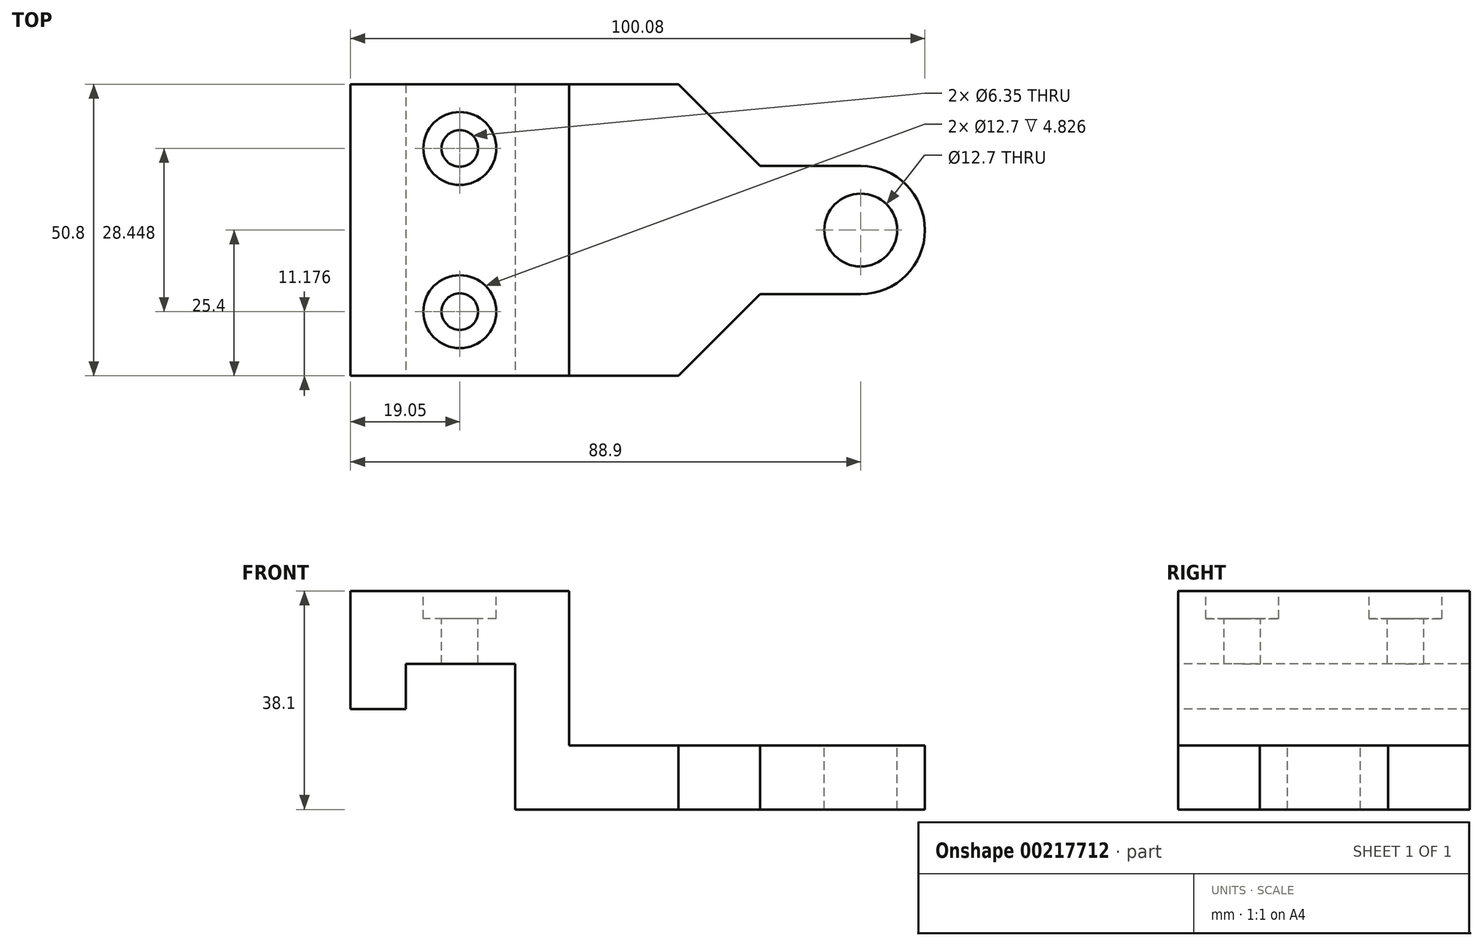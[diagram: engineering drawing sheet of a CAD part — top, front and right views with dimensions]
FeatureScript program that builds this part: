
annotation { "Feature Type Name" : "Feature", "Feature Type Description" : "" }
export const myFeature = defineFeature(function(context is Context, id is Id, definition is map)
    precondition{}
    {
        {
            var Q0;
            Q0=qCreatedBy(makeId("Right.planeOp"),FACE);
            var sketch = newSketch(context, id + "F0", { "sketchPlane" : qUnion([Q0])});
            skLineSegment(sketch, "E0.bottom", {"start": v(25.4, -19.05) * mm, "end": v(-25.4, -19.05) * mm});
            skLineSegment(sketch, "E0.top", {"start": v(25.4, 19.05) * mm, "end": v(-25.4, 19.05) * mm});
            skLineSegment(sketch, "E0.left", {"start": v(25.4, -19.05) * mm, "end": v(25.4, 19.05) * mm});
            skLineSegment(sketch, "E0.right", {"start": v(-25.4, -19.05) * mm, "end": v(-25.4, 19.05) * mm});
            skPoint(sketch, "E0.middle", {"position": v(0, 0) * mm});
            skSolve(sketch);
        }
        {
            var Q0;
            Q0=makeQuery(id+"F0.imprint","IMPRINT",FACE,{"disambiguationData":[TD([[makeQuery(id+"F0.imprint","IMPRINT",EDGE,{"derivedFrom":sQuery(id+"F0.wireOp",EDGE,"E0.bottom")}),-1.0]])]});
            extrude(context, id + "F1", {"entities" : qUnion([Q0]), "endBound" : BoundingType.SYMMETRIC, "depth" : 101.6 * mm});
        }
        {
            var Q0;
            Q0=makeQuery(id+"F1.opExtrude","SWEPT_FACE",FACE,{"disambiguationData":[OSD([sQuery(id+"F0.wireOp",EDGE,"E0.top")])]});
            var sketch = newSketch(context, id + "F2", { "sketchPlane" : qUnion([Q0])});
            skCircle(sketch, "E1", {"center": v(-31.75, -14.22) * mm, "radius": 3.18 * mm});
            skCircle(sketch, "E2", {"center": v(-31.75, 14.22) * mm, "radius": 3.18 * mm});
            skSolve(sketch);
        }
        {
            var Q0;
            Q0=makeQuery(id+"F2.imprint","IMPRINT",FACE,{"disambiguationData":[TD([[makeQuery(id+"F2.imprint","IMPRINT",EDGE,{"derivedFrom":sQuery(id+"F2.wireOp",EDGE,"E1")}),1.0]])]});
            var Q1;
            Q1=makeQuery(id+"F2.imprint","IMPRINT",FACE,{"disambiguationData":[TD([[makeQuery(id+"F2.imprint","IMPRINT",EDGE,{"derivedFrom":sQuery(id+"F2.wireOp",EDGE,"E2")}),1.0]])]});
            extrude(context, id + "F3", {"entities" : qUnion([Q0, Q1]), "operationType" : NewBodyOperationType.REMOVE, "endBound" : BoundingType.THROUGH_ALL, "oppositeDirection" : true, "depth" : 25.4 * mm});
        }
        {
            var Q0;
            Q0=makeQuery(id+"F1.opExtrude","SWEPT_FACE",FACE,{"disambiguationData":[OSD([sQuery(id+"F0.wireOp",EDGE,"E0.right")])]});
            var sketch = newSketch(context, id + "F4", { "sketchPlane" : qUnion([Q0])});
            skLineSegment(sketch, "E3", {"start": v(-50.8, 19.05) * mm, "end": v(-50.8, -1.52) * mm});
            skLineSegment(sketch, "E4", {"start": v(-50.8, -1.52) * mm, "end": v(-41.15, -1.52) * mm});
            skLineSegment(sketch, "E5", {"start": v(-50.8, 19.05) * mm, "end": v(-12.7, 19.05) * mm});
            skLineSegment(sketch, "E6", {"start": v(-12.7, -7.87) * mm, "end": v(50.8, -7.87) * mm});
            skLineSegment(sketch, "E7", {"start": v(50.8, -7.87) * mm, "end": v(50.8, 19.05) * mm});
            skLineSegment(sketch, "E8", {"start": v(50.8, 19.05) * mm, "end": v(-12.7, 19.05) * mm});
            skLineSegment(sketch, "E9", {"start": v(-41.15, -1.52) * mm, "end": v(-41.15, 6.35) * mm});
            skLineSegment(sketch, "E10", {"start": v(-41.15, 6.35) * mm, "end": v(-22.1, 6.35) * mm});
            skLineSegment(sketch, "E11", {"start": v(-22.1, 6.35) * mm, "end": v(-22.1, -19.05) * mm});
            skLineSegment(sketch, "E12", {"start": v(-22.1, -19.05) * mm, "end": v(-12.7, -19.05) * mm});
            skLineSegment(sketch, "E13", {"start": v(-12.7, -7.87) * mm, "end": v(-12.7, 19.05) * mm});
            skSolve(sketch);
        }
        {
            var Q0;
            {var subQ1=sQuery(id+"F4.wireOp",EDGE,"E4");Q0=makeQuery(id+"F4.imprint","IMPRINT",FACE,{"disambiguationData":[TD([[makeQuery(id+"F4.imprint","IMPRINT",EDGE,{"derivedFrom":subQ1}),-1.0]])]});}
            var Q1;
            Q1=makeQuery(id+"F4.imprint","IMPRINT",FACE,{"disambiguationData":[TD([[makeQuery(id+"F4.imprint","IMPRINT",EDGE,{"derivedFrom":sQuery(id+"F4.wireOp",EDGE,"E6")}),1.0]])]});
            extrude(context, id + "F5", {"entities" : qUnion([Q0, Q1]), "operationType" : NewBodyOperationType.REMOVE, "endBound" : BoundingType.THROUGH_ALL, "oppositeDirection" : true, "depth" : 25.4 * mm});
        }
        {
            var Q0;
            Q0=makeQuery(id+"F5.boolean.opBoolean","COPY",FACE,{"derivedFrom":makeQuery(id+"F5.opExtrude","SWEPT_FACE",FACE,{"disambiguationData":[OSD([sQuery(id+"F4.wireOp",EDGE,"E6")])]})});
            var sketch = newSketch(context, id + "F6", { "sketchPlane" : qUnion([Q0])});
            skPoint(sketch, "E14.endSnap0", {"position": v(-12.7, 0) * mm});
            skCircle(sketch, "E15", {"center": v(38.1, 0) * mm, "radius": 6.35 * mm});
            skArc(sketch, "E16", {"start": v(38.1, -11.18) * mm, "mid": v(49.28, 0) * mm, "end": v(38.1, 11.18) * mm});
            skLineSegment(sketch, "E17", {"start": v(-12.7, -25.4) * mm, "end": v(6.35, -25.4) * mm});
            skLineSegment(sketch, "E18", {"start": v(6.35, -25.4) * mm, "end": v(6.35, 25.4) * mm});
            skLineSegment(sketch, "E19", {"start": v(38.1, -11.18) * mm, "end": v(20.57, -11.18) * mm});
            skLineSegment(sketch, "E20", {"start": v(38.1, 11.18) * mm, "end": v(24.5, 11.18) * mm});
            skLineSegment(sketch, "E21", {"start": v(20.57, -11.18) * mm, "end": v(6.35, -25.4) * mm});
            skLineSegment(sketch, "E22", {"start": v(20.57, -11.18) * mm, "end": v(20.57, 11.18) * mm});
            skLineSegment(sketch, "E23", {"start": v(24.5, 11.18) * mm, "end": v(20.57, 11.18) * mm});
            skLineSegment(sketch, "E24", {"start": v(6.35, 25.4) * mm, "end": v(20.57, 11.18) * mm});
            skSolve(sketch);
        }
        {
            var Q0;
            Q0=makeQuery(id+"F6.imprint","IMPRINT",FACE,{"disambiguationData":[TD([[makeQuery(id+"F6.imprint","IMPRINT",EDGE,{"derivedFrom":sQuery(id+"F6.wireOp",EDGE,"E16")}),-1.0]])]});
            var Q1;
            Q1=makeQuery(id+"F6.imprint","IMPRINT",FACE,{"disambiguationData":[TD([[makeQuery(id+"F6.imprint","IMPRINT",EDGE,{"derivedFrom":sQuery(id+"F6.wireOp",EDGE,"E15")}),1.0]])]});
            extrude(context, id + "F7", {"entities" : qUnion([Q0, Q1]), "operationType" : NewBodyOperationType.REMOVE, "endBound" : BoundingType.THROUGH_ALL, "oppositeDirection" : true, "depth" : 25.4 * mm});
        }
        {
            var Q0;
            Q0=makeQuery(id+"F1.opExtrude","SWEPT_FACE",FACE,{"disambiguationData":[OSD([sQuery(id+"F0.wireOp",EDGE,"E0.top")])]});
            var sketch = newSketch(context, id + "F8", { "sketchPlane" : qUnion([Q0])});
            skCircle(sketch, "E25", {"center": v(-31.75, 14.22) * mm, "radius": 6.35 * mm});
            skCircle(sketch, "E26", {"center": v(-31.75, -14.22) * mm, "radius": 6.35 * mm});
            skSolve(sketch);
        }
        {
            var Q0;
            Q0=makeQuery(id+"F8.imprint","IMPRINT",FACE,{"disambiguationData":[TD([[makeQuery(id+"F8.imprint","IMPRINT",EDGE,{"derivedFrom":sQuery(id+"F8.wireOp",EDGE,"E25")}),1.0]])]});
            var Q1;
            Q1=makeQuery(id+"F8.imprint","IMPRINT",FACE,{"disambiguationData":[TD([[makeQuery(id+"F8.imprint","IMPRINT",EDGE,{"derivedFrom":sQuery(id+"F8.wireOp",EDGE,"E26")}),1.0]])]});
            extrude(context, id + "F9", {"entities" : qUnion([Q0, Q1]), "operationType" : NewBodyOperationType.REMOVE, "oppositeDirection" : true, "depth" : 4.83 * mm});
        }
    });
